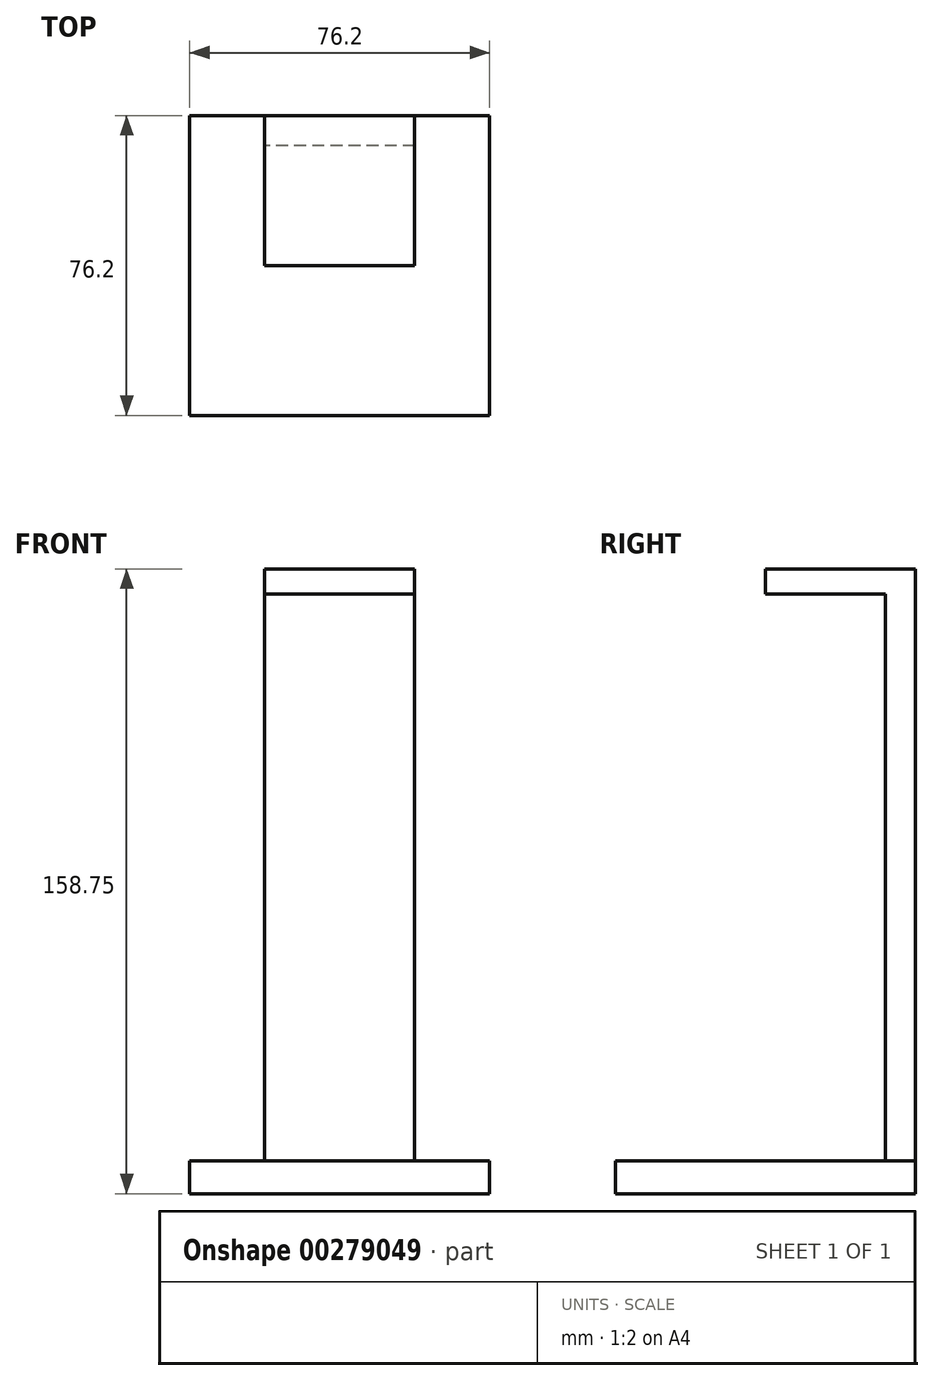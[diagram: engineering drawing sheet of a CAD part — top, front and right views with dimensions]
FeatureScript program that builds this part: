
annotation { "Feature Type Name" : "Feature", "Feature Type Description" : "" }
export const myFeature = defineFeature(function(context is Context, id is Id, definition is map)
    precondition{}
    {
        {
            var Q0;
            Q0=qCreatedBy(makeId("Front.planeOp"),FACE);
            var sketch = newSketch(context, id + "F0", { "sketchPlane" : qUnion([Q0])});
            skLineSegment(sketch, "E0.bottom", {"start": v(38.1, -4.2) * mm, "end": v(-38.1, -4.2) * mm});
            skLineSegment(sketch, "E0.top", {"start": v(38.1, 4.2) * mm, "end": v(-38.1, 4.2) * mm});
            skLineSegment(sketch, "E0.left", {"start": v(38.1, -4.2) * mm, "end": v(38.1, 4.2) * mm});
            skLineSegment(sketch, "E0.right", {"start": v(-38.1, -4.2) * mm, "end": v(-38.1, 4.2) * mm});
            skPoint(sketch, "E0.middle", {"position": v(0, 0) * mm});
            skSolve(sketch);
        }
        {
            var Q0;
            Q0 = qSketchRegion(id + "F0", true);
            extrude(context, id + "F1", {"entities" : qUnion([Q0]), "depth" : 76.2 * mm});
        }
        {
            var Q0;
            Q0=qCreatedBy(makeId("Front.planeOp"),FACE);
            var sketch = newSketch(context, id + "F2", { "sketchPlane" : qUnion([Q0])});
            skLineSegment(sketch, "E1.bottom", {"start": v(19.05, -4.2) * mm, "end": v(-19.05, -4.2) * mm});
            skLineSegment(sketch, "E1.top", {"start": v(19.05, 148.2) * mm, "end": v(-19.05, 148.2) * mm});
            skLineSegment(sketch, "E1.left", {"start": v(19.05, -4.2) * mm, "end": v(19.05, 148.2) * mm});
            skLineSegment(sketch, "E1.right", {"start": v(-19.05, -4.2) * mm, "end": v(-19.05, 148.2) * mm});
            skSolve(sketch);
        }
        {
            var Q0;
            Q0 = qSketchRegion(id + "F2", true);
            extrude(context, id + "F3", {"entities" : qUnion([Q0]), "operationType" : NewBodyOperationType.ADD, "depth" : 7.62 * mm});
        }
        {
            var Q0;
            Q0=makeQuery(id+"F3.opExtrude","SWEPT_FACE",FACE,{"disambiguationData":[OSD([sQuery(id+"F2.wireOp",EDGE,"E1.top")])]});
            var sketch = newSketch(context, id + "F4", { "sketchPlane" : qUnion([Q0])});
            skLineSegment(sketch, "E2.bottom", {"start": v(-19.05, 0) * mm, "end": v(19.05, 0) * mm});
            skLineSegment(sketch, "E2.top", {"start": v(-19.05, -38.1) * mm, "end": v(19.05, -38.1) * mm});
            skLineSegment(sketch, "E2.left", {"start": v(-19.05, 0) * mm, "end": v(-19.05, -38.1) * mm});
            skLineSegment(sketch, "E2.right", {"start": v(19.05, 0) * mm, "end": v(19.05, -38.1) * mm});
            skSolve(sketch);
        }
        {
            var Q0;
            Q0 = qSketchRegion(id + "F4", true);
            extrude(context, id + "F5", {"entities" : qUnion([Q0]), "operationType" : NewBodyOperationType.ADD, "depth" : 6.35 * mm});
        }
    });
